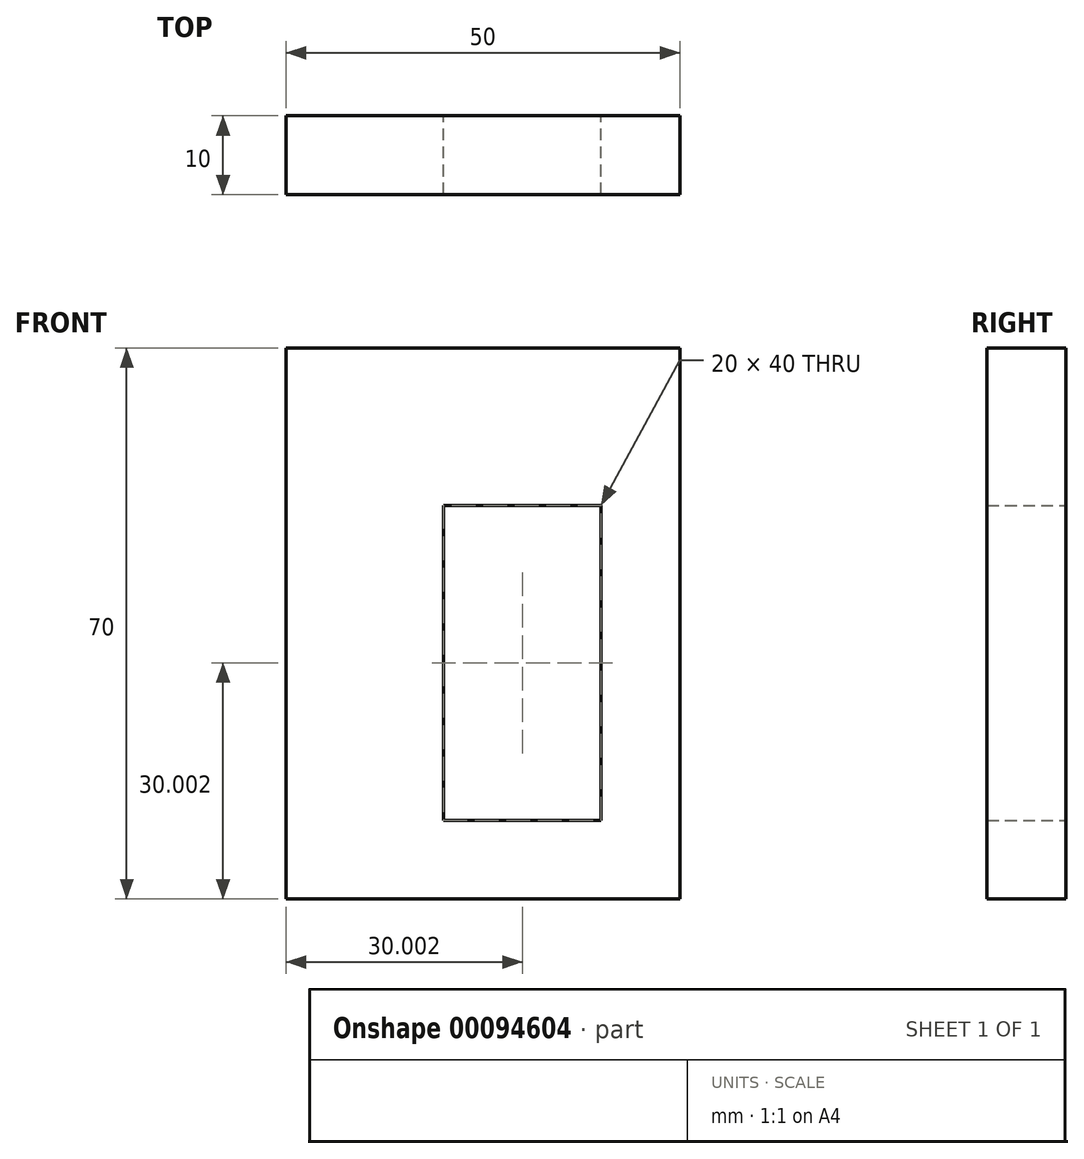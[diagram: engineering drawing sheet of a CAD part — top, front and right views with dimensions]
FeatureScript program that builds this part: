
annotation { "Feature Type Name" : "Feature", "Feature Type Description" : "" }
export const myFeature = defineFeature(function(context is Context, id is Id, definition is map)
    precondition{}
    {
        {
            var Q0;
            Q0=qCreatedBy(makeId("Front.planeOp"),FACE);
            var sketch = newSketch(context, id + "F0", { "sketchPlane" : qUnion([Q0])});
            skLineSegment(sketch, "E0", {"start": v(-50, 40) * mm, "end": v(-50, -30) * mm});
            skLineSegment(sketch, "E1", {"start": v(-50, -30) * mm, "end": v(0, -30) * mm});
            skLineSegment(sketch, "E2", {"start": v(0, -30) * mm, "end": v(0, 40) * mm});
            skLineSegment(sketch, "E3", {"start": v(0, 40) * mm, "end": v(-50, 40) * mm});
            skLineSegment(sketch, "E4", {"start": v(-10, -20) * mm, "end": v(-10, 20) * mm});
            skLineSegment(sketch, "E5", {"start": v(-10, -20) * mm, "end": v(-30, -20) * mm});
            skLineSegment(sketch, "E6", {"start": v(-30, -20) * mm, "end": v(-30, 20) * mm});
            skLineSegment(sketch, "E7", {"start": v(-30, 20) * mm, "end": v(-10, 20) * mm});
            skSolve(sketch);
        }
        {
            var Q0;
            Q0 = qSketchRegion(id + "F0", true);
            extrude(context, id + "F1", {"entities" : qUnion([Q0]), "depth" : 10 * mm});
        }
    });
